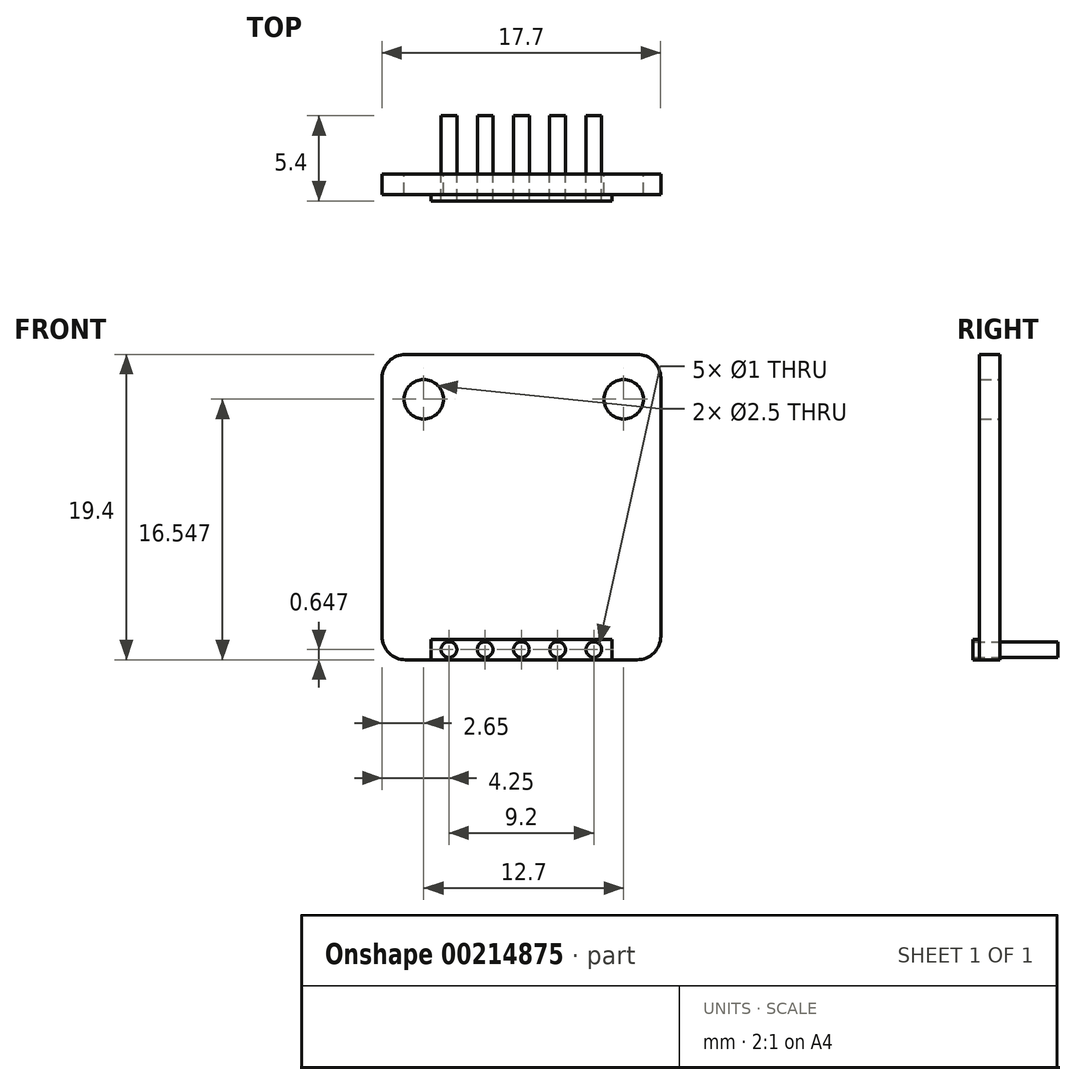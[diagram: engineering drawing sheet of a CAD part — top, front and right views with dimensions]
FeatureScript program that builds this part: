
annotation { "Feature Type Name" : "Feature", "Feature Type Description" : "" }
export const myFeature = defineFeature(function(context is Context, id is Id, definition is map)
    precondition{}
    {
        {
            var Q0;
            Q0=qCreatedBy(makeId("Front.planeOp"),FACE);
            var sketch = newSketch(context, id + "F0", { "sketchPlane" : qUnion([Q0])});
            skLineSegment(sketch, "E0", {"start": v(-27.72, -17.17) * mm, "end": v(-13.02, -17.17) * mm});
            skLineSegment(sketch, "E1", {"start": v(-11.52, -15.67) * mm, "end": v(-11.52, 0.73) * mm});
            skLineSegment(sketch, "E2", {"start": v(-29.22, -15.67) * mm, "end": v(-29.22, 0.73) * mm});
            skLineSegment(sketch, "E3", {"start": v(-27.72, 2.23) * mm, "end": v(-13.02, 2.23) * mm});
            skPoint(sketch, "E4.visualSharp", {"position": v(-29.22, 2.23) * mm});
            skArc(sketch, "E4.filletArc", {"start": v(-27.72, 2.23) * mm, "mid": v(-28.78, 1.79) * mm, "end": v(-29.22, 0.73) * mm});
            skPoint(sketch, "E5.visualSharp", {"position": v(-29.22, -17.17) * mm});
            skArc(sketch, "E5.filletArc", {"start": v(-29.22, -15.67) * mm, "mid": v(-28.78, -16.73) * mm, "end": v(-27.72, -17.17) * mm});
            skPoint(sketch, "E6.visualSharp", {"position": v(-11.52, -17.17) * mm});
            skArc(sketch, "E6.filletArc", {"start": v(-13.02, -17.17) * mm, "mid": v(-11.96, -16.73) * mm, "end": v(-11.52, -15.67) * mm});
            skPoint(sketch, "E7.visualSharp", {"position": v(-11.52, 2.23) * mm});
            skArc(sketch, "E7.filletArc", {"start": v(-11.52, 0.73) * mm, "mid": v(-11.96, 1.79) * mm, "end": v(-13.02, 2.23) * mm});
            skLineSegment(sketch, "E8", {"start": v(-11.52, 0.73) * mm, "end": v(-12.62, 0.73) * mm, "construction": true});
            skLineSegment(sketch, "E9", {"start": v(-12.62, 0.73) * mm, "end": v(-13.87, 0.73) * mm, "construction": true});
            skLineSegment(sketch, "E10", {"start": v(-13.87, 2.23) * mm, "end": v(-13.87, 0.63) * mm, "construction": true});
            skLineSegment(sketch, "E11", {"start": v(-13.87, 0.63) * mm, "end": v(-13.87, -0.62) * mm, "construction": true});
            skCircle(sketch, "E12", {"center": v(-13.87, -0.62) * mm, "radius": 1.25 * mm});
            skLineSegment(sketch, "E13", {"start": v(-13.87, -0.62) * mm, "end": v(-26.57, -0.62) * mm, "construction": true});
            skCircle(sketch, "E14", {"center": v(-26.57, -0.62) * mm, "radius": 1.25 * mm});
            skLineSegment(sketch, "E15", {"start": v(-14.62, -15.87) * mm, "end": v(-26.12, -15.87) * mm});
            skLineSegment(sketch, "E16", {"start": v(-26.12, -17.17) * mm, "end": v(-26.12, -15.87) * mm});
            skLineSegment(sketch, "E17", {"start": v(-26.12, -15.87) * mm, "end": v(-23.82, -15.87) * mm});
            skLineSegment(sketch, "E18", {"start": v(-23.82, -15.87) * mm, "end": v(-23.82, -17.17) * mm, "construction": true});
            skLineSegment(sketch, "E19", {"start": v(-23.82, -15.87) * mm, "end": v(-21.52, -15.87) * mm, "construction": true});
            skLineSegment(sketch, "E20", {"start": v(-21.52, -15.87) * mm, "end": v(-21.52, -17.17) * mm, "construction": true});
            skLineSegment(sketch, "E21", {"start": v(-21.52, -15.87) * mm, "end": v(-19.22, -15.87) * mm, "construction": true});
            skLineSegment(sketch, "E22", {"start": v(-19.22, -15.87) * mm, "end": v(-19.22, -17.17) * mm, "construction": true});
            skLineSegment(sketch, "E23", {"start": v(-19.22, -15.87) * mm, "end": v(-16.92, -15.87) * mm, "construction": true});
            skLineSegment(sketch, "E24", {"start": v(-16.92, -15.87) * mm, "end": v(-16.92, -17.17) * mm, "construction": true});
            skLineSegment(sketch, "E25", {"start": v(-16.92, -15.87) * mm, "end": v(-14.62, -15.87) * mm, "construction": true});
            skLineSegment(sketch, "E26", {"start": v(-14.62, -17.17) * mm, "end": v(-14.62, -15.87) * mm});
            skLineSegment(sketch, "E27", {"start": v(-24.97, -15.87) * mm, "end": v(-24.97, -17.17) * mm, "construction": true});
            skLineSegment(sketch, "E28", {"start": v(-22.67, -15.87) * mm, "end": v(-22.67, -17.17) * mm, "construction": true});
            skLineSegment(sketch, "E29", {"start": v(-20.37, -15.87) * mm, "end": v(-20.37, -17.17) * mm, "construction": true});
            skLineSegment(sketch, "E30", {"start": v(-18.07, -15.87) * mm, "end": v(-18.07, -17.17) * mm, "construction": true});
            skLineSegment(sketch, "E31", {"start": v(-15.77, -15.87) * mm, "end": v(-15.77, -17.17) * mm, "construction": true});
            skCircle(sketch, "E32", {"center": v(-24.97, -16.52) * mm, "radius": 0.5 * mm});
            skCircle(sketch, "E33", {"center": v(-22.67, -16.52) * mm, "radius": 0.5 * mm});
            skCircle(sketch, "E34", {"center": v(-20.37, -16.52) * mm, "radius": 0.5 * mm});
            skCircle(sketch, "E35", {"center": v(-18.07, -16.52) * mm, "radius": 0.5 * mm});
            skCircle(sketch, "E36", {"center": v(-15.77, -16.52) * mm, "radius": 0.5 * mm});
            skSolve(sketch);
        }
        {
            var Q0;
            Q0=makeQuery(id+"F0.imprint","IMPRINT",FACE,{"disambiguationData":[TD([[makeQuery(id+"F0.imprint","IMPRINT",EDGE,{"derivedFrom":sQuery(id+"F0.wireOp",EDGE,"E1")}),1.0]])]});
            extrude(context, id + "F1", {"entities" : qUnion([Q0]), "depth" : 1.3 * mm});
        }
        {
            var Q0;
            Q0=makeQuery(id+"F0.imprint","IMPRINT",FACE,{"disambiguationData":[TD([[makeQuery(id+"F0.imprint","IMPRINT",EDGE,{"derivedFrom":sQuery(id+"F0.wireOp",EDGE,"E15")}),1.0]])]});
            extrude(context, id + "F2", {"entities" : qUnion([Q0]), "operationType" : NewBodyOperationType.ADD, "depth" : 1.7 * mm});
        }
        {
            var Q0;
            Q0=makeQuery(id+"F0.imprint","IMPRINT",FACE,{"disambiguationData":[TD([[makeQuery(id+"F0.imprint","IMPRINT",EDGE,{"derivedFrom":sQuery(id+"F0.wireOp",EDGE,"E32")}),1.0]])]});
            var Q1;
            Q1=makeQuery(id+"F0.imprint","IMPRINT",FACE,{"disambiguationData":[TD([[makeQuery(id+"F0.imprint","IMPRINT",EDGE,{"derivedFrom":sQuery(id+"F0.wireOp",EDGE,"E33")}),1.0]])]});
            var Q2;
            Q2=makeQuery(id+"F0.imprint","IMPRINT",FACE,{"disambiguationData":[TD([[makeQuery(id+"F0.imprint","IMPRINT",EDGE,{"derivedFrom":sQuery(id+"F0.wireOp",EDGE,"E34")}),1.0]])]});
            var Q3;
            Q3=makeQuery(id+"F0.imprint","IMPRINT",FACE,{"disambiguationData":[TD([[makeQuery(id+"F0.imprint","IMPRINT",EDGE,{"derivedFrom":sQuery(id+"F0.wireOp",EDGE,"E35")}),1.0]])]});
            var Q4;
            Q4=makeQuery(id+"F0.imprint","IMPRINT",FACE,{"disambiguationData":[TD([[makeQuery(id+"F0.imprint","IMPRINT",EDGE,{"derivedFrom":sQuery(id+"F0.wireOp",EDGE,"E36")}),1.0]])]});
            extrude(context, id + "F3", {"entities" : qUnion([Q0, Q1, Q2, Q3, Q4]), "oppositeDirection" : true, "depth" : 3.7 * mm});
        }
    });
